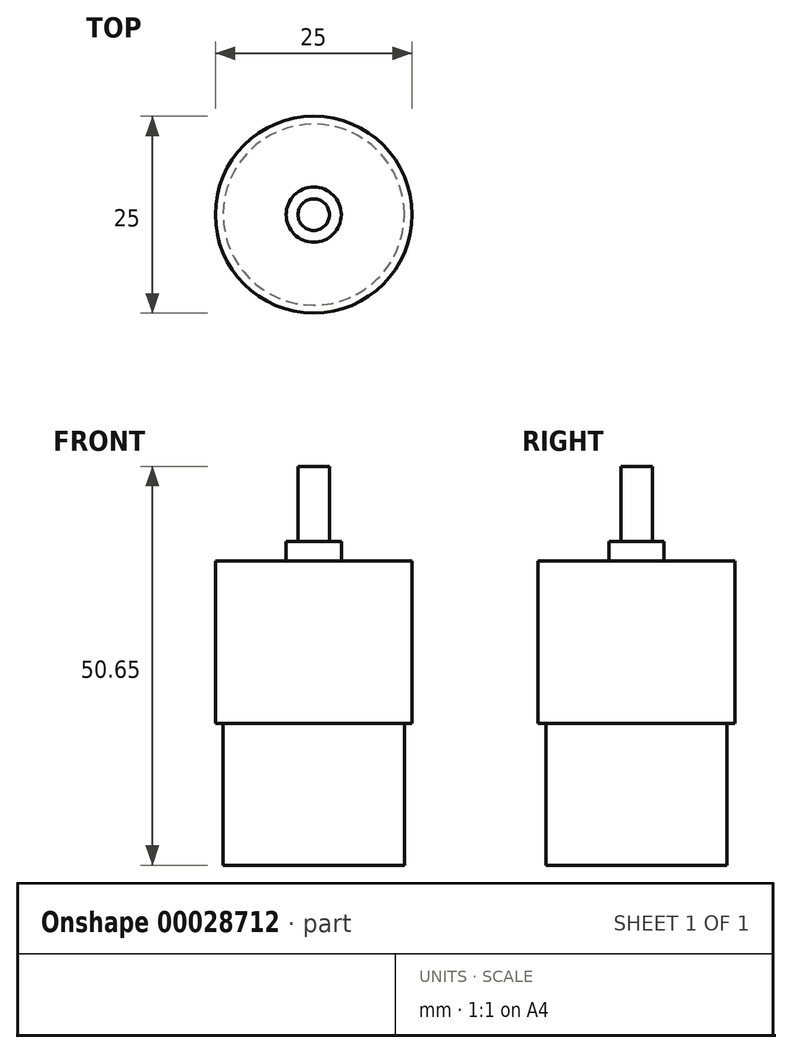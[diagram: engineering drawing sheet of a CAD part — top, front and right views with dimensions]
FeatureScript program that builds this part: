
annotation { "Feature Type Name" : "Feature", "Feature Type Description" : "" }
export const myFeature = defineFeature(function(context is Context, id is Id, definition is map)
    precondition{}
    {
        {
            var Q0;
            Q0=qCreatedBy(makeId("Front.planeOp"),FACE);
            var sketch = newSketch(context, id + "F0", { "sketchPlane" : qUnion([Q0])});
            skLineSegment(sketch, "E0", {"start": v(0, 0) * mm, "end": v(0, 64.91) * mm, "construction": true});
            skLineSegment(sketch, "E1", {"start": v(0, 50.65) * mm, "end": v(2, 50.65) * mm});
            skLineSegment(sketch, "E2", {"start": v(2, 50.65) * mm, "end": v(2, 41.15) * mm});
            skLineSegment(sketch, "E3", {"start": v(2, 41.15) * mm, "end": v(3.5, 41.15) * mm});
            skLineSegment(sketch, "E4", {"start": v(3.5, 41.15) * mm, "end": v(3.5, 38.65) * mm});
            skLineSegment(sketch, "E5", {"start": v(3.5, 38.65) * mm, "end": v(12.5, 38.65) * mm});
            skLineSegment(sketch, "E6", {"start": v(12.5, 38.65) * mm, "end": v(12.5, 18) * mm});
            skLineSegment(sketch, "E7", {"start": v(12.5, 18) * mm, "end": v(11.5, 18) * mm});
            skLineSegment(sketch, "E8", {"start": v(11.5, 18) * mm, "end": v(11.5, 0) * mm});
            skLineSegment(sketch, "E9", {"start": v(11.5, 0) * mm, "end": v(0, 0) * mm});
            skLineSegment(sketch, "E10", {"start": v(0, 50.65) * mm, "end": v(0, 0) * mm});
            skSolve(sketch);
        }
        {
            var Q0;
            Q0 = qSketchRegion(id + "F0", true);
            var Q1;
            Q1=sQuery(id+"F0.wireOp",EDGE,"E0");
            revolve(context, id + "F1", {"surfaceOperationType" : NewSurfaceOperationType.NEW, "entities" : qUnion([Q0]), "axis" : qUnion([Q1]), "revolveType" : RevolveType.FULL});
        }
    });
